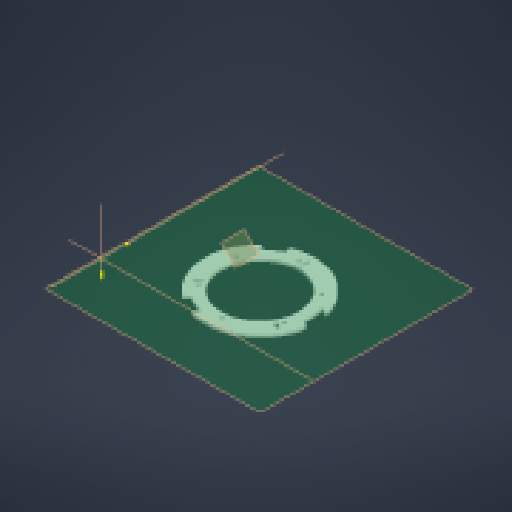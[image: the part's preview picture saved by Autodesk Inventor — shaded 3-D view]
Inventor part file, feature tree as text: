
AUTODESK INVENTOR PART (.ipt)
format: ipt  version: 2023 (Build 270158000, 158)  size: 249,856 bytes
history: native  units: mm
features: reference x16, other x11, sketch x6, extrude x3, plane x2
ambient origin geometry x8: Origin, YZ Plane, XZ Plane, XY Plane, X Axis, Y Axis, Z Axis, Center Point
bodies: Solid1 (feature_tree)
feature tree (38):
  plane  "Work Plane1"
  sketch  "Sketch1"  dims[d1=3.0mm d2=0.0mm d3=6.0mm]
  plane  "Work Plane2"
  extrude  "Extrusion1"  Depth=3.0mm
  sketch  "Sketch3"  dims[d6=4.5mm d7=4.5mm]
  extrude  "Extrusion2"  Depth=4.5mm
  sketch  "Sketch5"  dims[d9=4.5mm]
  extrude  "Extrusion3"  Depth=4.5mm
  sketch  "Sketch2"  dims[d4=4.5mm d5=4.5mm]
  reference  "Reference2"
  reference  "Reference4"
  reference  "Reference5"
  reference  "Reference6"
  reference  "Reference7"
  sketch  "Sketch4"  dims[d8=4.5mm]
  reference  "Reference8"
  reference  "Reference9"
  reference  "Reference10"
  reference  "Reference11"
  reference  "Reference12"
  reference  "Reference13"
  reference  "Reference14"
  reference  "Reference15"
  sketch  "Sketch6"  dims[d10=10.0mm d11=0.0mm d12=10.0mm d13=0.0mm]
  reference  "Reference16"
  reference  "Reference17"
  reference  "Reference18"
  parser-record x1  (decoder bookkeeping rows leaked as tree rows — omitted from the tree; the rows remain in map.json)
  other  "Assembly1.iam"
  other  "Spant:1"
  other  "Spant:3"
  other  "Spant:2"
  other  "vase_v2._tom:1"
  other  "top_centering_ring:1"
  other  "Spant2:2"
  other  "Spant2:1"
  other  "Spant2:3"
  other  "Assembly1"
note: 1 file-system path scrubbed to <path> (originals preserved in map.json)
